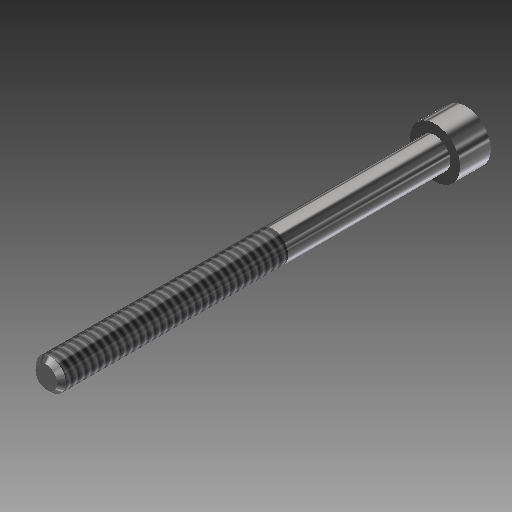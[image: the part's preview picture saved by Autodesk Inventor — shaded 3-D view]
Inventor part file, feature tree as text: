
AUTODESK INVENTOR PART (.ipt)
format: ipt  version: 2017 (Build 210142000, 142)  size: 136,704 bytes
history: native  units: in
note: dims shown in document units (in); Inventor stores cm internally (conversion verified against a paired STEP export)
features: extrude x3, sketch x3, chamfer x1, thread x1
ambient origin geometry x8: Origin, YZ Plane, XZ Plane, XY Plane, X Axis, Y Axis, Z Axis, Center Point
bodies: Solid1 (feature_tree)
feature tree (8):
  extrude  "Extrusion1"  Depth=1.75in TaperAngle=0.0deg
  extrude  "Extrusion2"  Depth=0.138in TaperAngle=0.0deg
  extrude  "Extrusion3"  Depth=0.069in TaperAngle=0.0deg
  chamfer  "Chamfer1"  Distance=0.02in Angle=45.0deg
  thread  "Thread2"  [1 undecoded]
  sketch  "Sketch1"  dims[d0=0.138in d1=1.75in d2=0.0in]
  sketch  "Sketch2"  dims[d3=0.226in d4=0.138in d5=0.0in]
  sketch  "Sketch3"  dims[d6=0.1094in d7=0.069in d8=0.0in d11=0.02in d12=0.125in d13=45.0deg d14=1.0in d15=0.0in]
note: 1 required parameter value undecoded (feature->parameter linkage not recoverable at this tier; creation-order binding heuristic only, values carry confidence <= 0.55)
